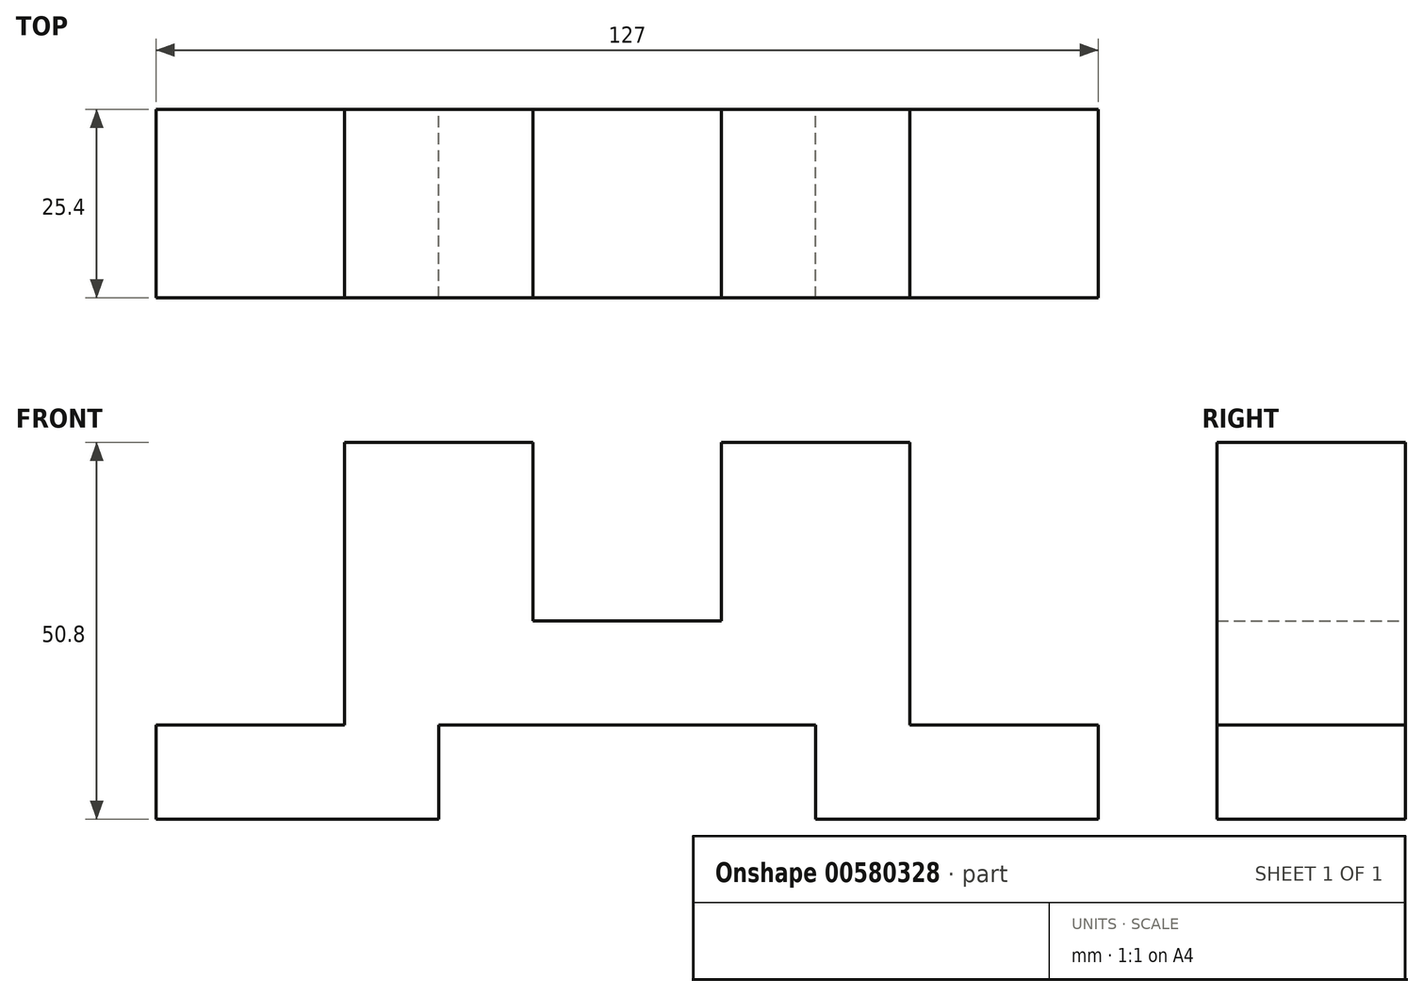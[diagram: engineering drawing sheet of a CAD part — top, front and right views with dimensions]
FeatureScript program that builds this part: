
annotation { "Feature Type Name" : "Feature", "Feature Type Description" : "" }
export const myFeature = defineFeature(function(context is Context, id is Id, definition is map)
    precondition{}
    {
        {
            var Q0;
            Q0=qCreatedBy(makeId("Front.planeOp"),FACE);
            var sketch = newSketch(context, id + "F0", { "sketchPlane" : qUnion([Q0])});
            skLineSegment(sketch, "E0", {"start": v(-58.38, -2.23) * mm, "end": v(-58.38, -14.93) * mm});
            skLineSegment(sketch, "E1", {"start": v(30.52, -2.23) * mm, "end": v(30.52, -14.93) * mm});
            skLineSegment(sketch, "E2", {"start": v(30.52, -14.93) * mm, "end": v(68.62, -14.93) * mm});
            skLineSegment(sketch, "E3", {"start": v(68.62, -14.93) * mm, "end": v(68.62, -2.23) * mm});
            skLineSegment(sketch, "E4", {"start": v(68.62, -2.23) * mm, "end": v(43.22, -2.23) * mm});
            skLineSegment(sketch, "E5", {"start": v(43.22, -2.23) * mm, "end": v(43.22, 35.87) * mm});
            skLineSegment(sketch, "E6", {"start": v(43.22, 35.87) * mm, "end": v(17.82, 35.87) * mm});
            skLineSegment(sketch, "E7", {"start": v(17.82, 35.87) * mm, "end": v(17.82, 11.8) * mm});
            skLineSegment(sketch, "E8", {"start": v(17.82, 11.8) * mm, "end": v(-7.58, 11.8) * mm});
            skLineSegment(sketch, "E9", {"start": v(-7.58, 11.8) * mm, "end": v(-7.58, 35.87) * mm});
            skLineSegment(sketch, "E10", {"start": v(-7.58, 35.87) * mm, "end": v(-32.98, 35.87) * mm});
            skLineSegment(sketch, "E11", {"start": v(-32.98, 35.87) * mm, "end": v(-32.98, -2.23) * mm});
            skLineSegment(sketch, "E12", {"start": v(-58.38, -2.23) * mm, "end": v(-32.98, -2.23) * mm});
            skPoint(sketch, "E13.trimOffspring.end.orphan", {"position": v(-27.85, 0) * mm});
            skLineSegment(sketch, "E14", {"start": v(-58.38, -14.93) * mm, "end": v(-20.28, -14.93) * mm});
            skLineSegment(sketch, "E15", {"start": v(-20.28, -14.93) * mm, "end": v(-20.28, -2.23) * mm});
            skLineSegment(sketch, "E16", {"start": v(-20.28, -2.23) * mm, "end": v(30.52, -2.23) * mm});
            skSolve(sketch);
        }
        {
            var Q0;
            Q0 = qSketchRegion(id + "F0", true);
            extrude(context, id + "F1", {"entities" : qUnion([Q0]), "depth" : 25.4 * mm, "offsetDistance" : 25.4 * mm});
        }
    });
